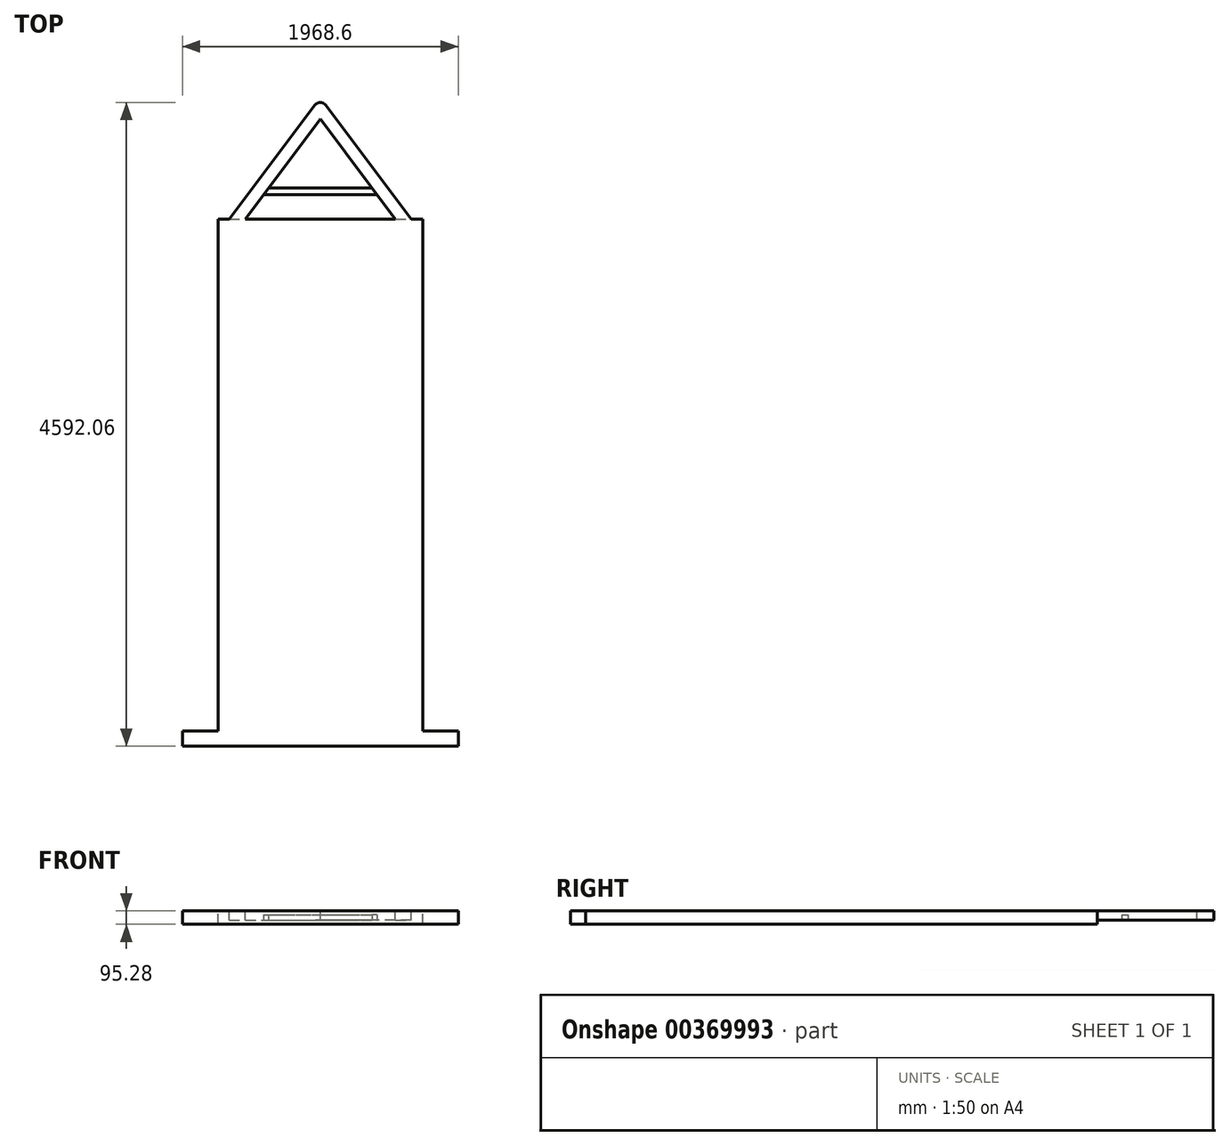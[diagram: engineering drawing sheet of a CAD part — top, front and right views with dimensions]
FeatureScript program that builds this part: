
annotation { "Feature Type Name" : "Feature", "Feature Type Description" : "" }
export const myFeature = defineFeature(function(context is Context, id is Id, definition is map)
    precondition{}
    {
        {
            var Q0;
            Q0=qCreatedBy(makeId("Front.planeOp"),FACE);
            var sketch = newSketch(context, id + "F0", { "sketchPlane" : qUnion([Q0])});
            skLineSegment(sketch, "E0.bottom", {"start": v(-110.16, -116.54) * mm, "end": v(1325.04, -116.54) * mm});
            skLineSegment(sketch, "E0.top", {"start": v(-110.16, -21.26) * mm, "end": v(1325.04, -21.26) * mm});
            skLineSegment(sketch, "E0.left", {"start": v(-110.16, -116.54) * mm, "end": v(-110.16, -21.26) * mm});
            skLineSegment(sketch, "E0.right", {"start": v(1325.04, -116.54) * mm, "end": v(1325.04, -21.26) * mm});
            skSolve(sketch);
        }
        {
            var Q0;
            Q0=makeQuery(id+"F0.imprint","IMPRINT",FACE,{"disambiguationData":[TD([[makeQuery(id+"F0.imprint","IMPRINT",EDGE,{"derivedFrom":sQuery(id+"F0.wireOp",EDGE,"E0.bottom")}),1.0]])]});
            extrude(context, id + "F1", {"entities" : qUnion([Q0]), "depth" : 3759.2 * mm});
        }
        {
            var Q0;
            Q0=makeQuery(id+"F1.opExtrude","SWEPT_FACE",FACE,{"disambiguationData":[OSD([sQuery(id+"F0.wireOp",EDGE,"E0.right")])]});
            extrude(context, id + "F2", {"entities" : qUnion([Q0]), "operationType" : NewBodyOperationType.ADD, "depth" : 25.4 * mm});
        }
        {
            var Q0;
            Q0=makeQuery(id+"F2.opExtrude","CAP_FACE",FACE,{"disambiguationData":[OSD([sQuery(id+"F0.wireOp",EDGE,"E0.right")])],"isStart":false});
            var sketch = newSketch(context, id + "F3", { "sketchPlane" : qUnion([Q0])});
            skLineSegment(sketch, "E1.bottom", {"start": v(-3759.2, -116.54) * mm, "end": v(-3651.2, -116.54) * mm});
            skLineSegment(sketch, "E1.top", {"start": v(-3759.2, -21.26) * mm, "end": v(-3651.2, -21.26) * mm});
            skLineSegment(sketch, "E1.left", {"start": v(-3759.2, -116.54) * mm, "end": v(-3759.2, -21.26) * mm});
            skLineSegment(sketch, "E1.right", {"start": v(-3651.2, -116.54) * mm, "end": v(-3651.2, -21.26) * mm});
            skSolve(sketch);
        }
        {
            var Q0;
            Q0=makeQuery(id+"F3.imprint","IMPRINT",FACE,{"disambiguationData":[TD([[makeQuery(id+"F3.imprint","IMPRINT",EDGE,{"derivedFrom":sQuery(id+"F3.wireOp",EDGE,"E1.bottom")}),1.0]])]});
            extrude(context, id + "F4", {"entities" : qUnion([Q0]), "operationType" : NewBodyOperationType.ADD, "depth" : 254 * mm});
        }
        {
            var Q0;
            Q0=makeQuery(id+"F1.opExtrude","SWEPT_FACE",FACE,{"disambiguationData":[OSD([sQuery(id+"F0.wireOp",EDGE,"E0.left")])]});
            var sketch = newSketch(context, id + "F5", { "sketchPlane" : qUnion([Q0])});
            skLineSegment(sketch, "E2.bottom", {"start": v(3759.2, -116.54) * mm, "end": v(3651.74, -116.54) * mm});
            skLineSegment(sketch, "E2.top", {"start": v(3759.2, -21.26) * mm, "end": v(3651.74, -21.26) * mm});
            skLineSegment(sketch, "E2.left", {"start": v(3759.2, -116.54) * mm, "end": v(3759.2, -21.26) * mm});
            skLineSegment(sketch, "E2.right", {"start": v(3651.74, -116.54) * mm, "end": v(3651.74, -21.26) * mm});
            skSolve(sketch);
        }
        {
            var Q0;
            Q0=makeQuery(id+"F5.imprint","IMPRINT",FACE,{"disambiguationData":[TD([[makeQuery(id+"F5.imprint","IMPRINT",EDGE,{"derivedFrom":sQuery(id+"F5.wireOp",EDGE,"E2.bottom")}),-1.0]])]});
            extrude(context, id + "F6", {"entities" : qUnion([Q0]), "operationType" : NewBodyOperationType.ADD, "depth" : 254 * mm});
        }
        {
            var Q0;
            {var subQ0=sQuery(id+"F0.wireOp",EDGE,"E0.top");Q0=makeQuery(id+"F6.boolean.opBoolean","MERGE",FACE,{"derivedFrom":[makeQuery(id+"F4.boolean.opBoolean","MERGE",FACE,{"derivedFrom":[makeQuery(id+"F2.boolean.opBoolean","MERGE",FACE,{"derivedFrom":[makeQuery(id+"F1.opExtrude","SWEPT_FACE",FACE,{"disambiguationData":[OSD([subQ0])]}),makeQuery(id+"F2.opExtrude","SWEPT_FACE",FACE,{"disambiguationData":[OSD([subQ0,sQuery(id+"F0.wireOp",EDGE,"E0.right")])]})]}),makeQuery(id+"F4.opExtrude","SWEPT_FACE",FACE,{"disambiguationData":[OSD([sQuery(id+"F3.wireOp",EDGE,"E1.top")])]})]}),makeQuery(id+"F6.opExtrude","SWEPT_FACE",FACE,{"disambiguationData":[OSD([sQuery(id+"F5.wireOp",EDGE,"E2.top")])]})]});}
            var sketch = newSketch(context, id + "F7", { "sketchPlane" : qUnion([Q0])});
            skPoint(sketch, "E3", {"position": v(620.14, 0) * mm});
            skLineSegment(sketch, "E4", {"start": v(620.14, 0) * mm, "end": v(620.14, 713.89) * mm, "construction": true});
            skLineSegment(sketch, "E5", {"start": v(1270.5, 0) * mm, "end": v(620.14, 866.7) * mm});
            skLineSegment(sketch, "E6.MirrorCS", {"start": v(-30.23, 0) * mm, "end": v(620.14, 866.7) * mm});
            skLineSegment(sketch, "E7", {"start": v(84.45, 0) * mm, "end": v(620.14, 713.89) * mm});
            skLineSegment(sketch, "E8.MirrorCS", {"start": v(1155.83, 0) * mm, "end": v(620.14, 713.89) * mm});
            skSolve(sketch);
        }
        {
            var Q0;
            {var subQ6=sQuery(id+"F7.wireOp",EDGE,"E5");Q0=makeQuery(id+"F7.imprint","IMPRINT",FACE,{"disambiguationData":[TD([[makeQuery(id+"F7.imprint","IMPRINT",EDGE,{"derivedFrom":subQ6}),1.0]])]});}
            extrude(context, id + "F8", {"entities" : qUnion([Q0]), "operationType" : NewBodyOperationType.ADD, "oppositeDirection" : true, "depth" : 64.37 * mm});
        }
        {
            var Q0;
            Q0=makeQuery(id+"F8.opExtrude","SWEPT_EDGE",EDGE,{"disambiguationData":[OSD([sQuery(id+"F7.wireOp",EDGE,"E5"),sQuery(id+"F7.wireOp",EDGE,"E6.MirrorCS")])]});
            fillet(context, id + "F9", {"entities" : qUnion([Q0]), "radius" : 50.8 * mm, "tangentPropagation" : true, "allowEdgeOverflow" : false});
        }
        {
            var Q0;
            Q0=makeQuery(id+"F8.opExtrude","CAP_FACE",FACE,{"disambiguationData":[OSD([sQuery(id+"F0.wireOp",EDGE,"E0.top"),sQuery(id+"F0.wireOp",EDGE,"E0.right"),sQuery(id+"F7.wireOp",EDGE,"E5"),sQuery(id+"F7.wireOp",EDGE,"E6.MirrorCS"),sQuery(id+"F7.wireOp",EDGE,"E7"),sQuery(id+"F7.wireOp",EDGE,"E8.MirrorCS")])],"isStart":false});
            var sketch = newSketch(context, id + "F10", { "sketchPlane" : qUnion([Q0])});
            skLineSegment(sketch, "E9", {"start": v(215.94, -175.23) * mm, "end": v(1024.34, -175.23) * mm});
            skLineSegment(sketch, "E10", {"start": v(250.9, -221.8) * mm, "end": v(989.39, -221.8) * mm});
            skLineSegment(sketch, "E11", {"start": v(989.39, -221.8) * mm, "end": v(1024.34, -175.23) * mm});
            skLineSegment(sketch, "E12", {"start": v(215.94, -175.23) * mm, "end": v(250.9, -221.8) * mm});
            skSolve(sketch);
        }
        {
            var Q0;
            Q0=makeQuery(id+"F10.imprint","IMPRINT",FACE,{"disambiguationData":[TD([[makeQuery(id+"F10.imprint","IMPRINT",EDGE,{"derivedFrom":sQuery(id+"F10.wireOp",EDGE,"E9")}),-1.0]])]});
            extrude(context, id + "F11", {"entities" : qUnion([Q0]), "operationType" : NewBodyOperationType.ADD, "oppositeDirection" : true, "depth" : 37.76 * mm});
        }
    });
